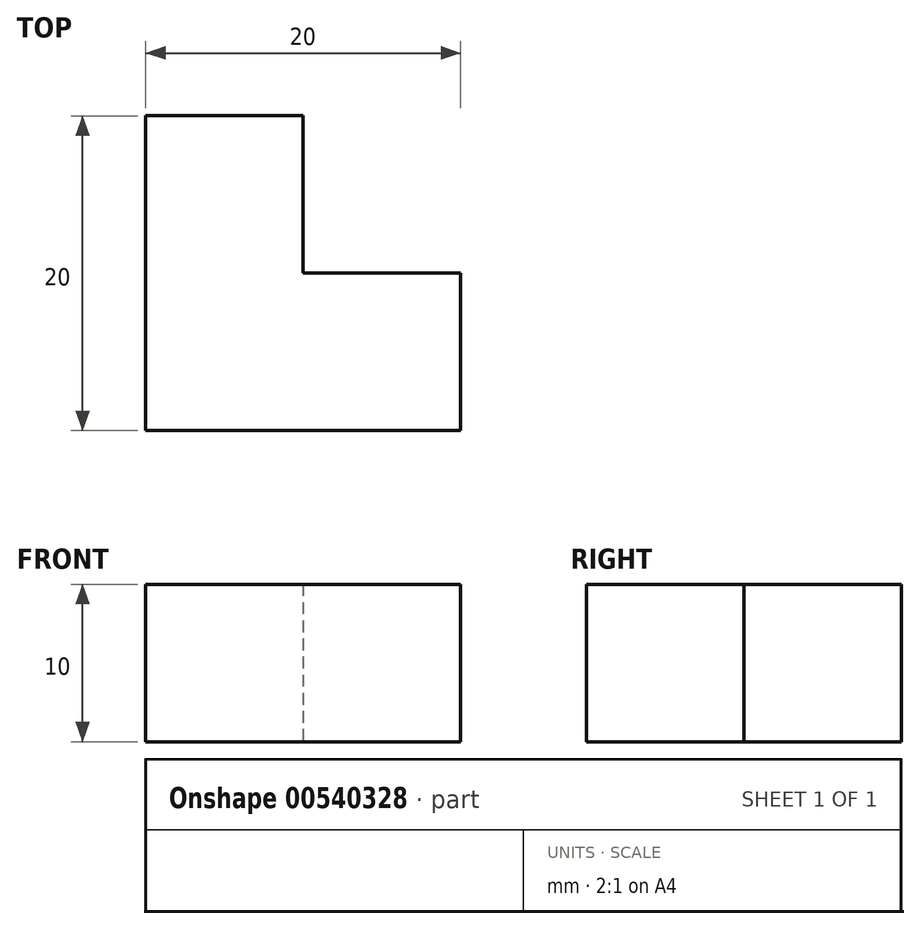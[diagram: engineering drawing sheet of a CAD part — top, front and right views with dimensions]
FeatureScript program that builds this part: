
annotation { "Feature Type Name" : "Feature", "Feature Type Description" : "" }
export const myFeature = defineFeature(function(context is Context, id is Id, definition is map)
    precondition{}
    {
        {
            var Q0;
            Q0=qCreatedBy(makeId("Top.planeOp"),FACE);
            var sketch = newSketch(context, id + "F0", { "sketchPlane" : qUnion([Q0])});
            skLineSegment(sketch, "E0", {"start": v(-20, 12.26) * mm, "end": v(-10, 12.26) * mm});
            skLineSegment(sketch, "E1", {"start": v(-10, 12.26) * mm, "end": v(-10, 2.26) * mm});
            skLineSegment(sketch, "E2", {"start": v(-10, 2.26) * mm, "end": v(0, 2.26) * mm});
            skLineSegment(sketch, "E3", {"start": v(0, 2.26) * mm, "end": v(0, -7.74) * mm});
            skLineSegment(sketch, "E4", {"start": v(0, -7.74) * mm, "end": v(-20, -7.74) * mm});
            skLineSegment(sketch, "E5", {"start": v(-20, -7.74) * mm, "end": v(-20, 12.26) * mm});
            skSolve(sketch);
        }
        {
            var Q0;
            Q0=makeQuery(id+"F0.imprint","IMPRINT",FACE,{"disambiguationData":[TD([[makeQuery(id+"F0.imprint","IMPRINT",EDGE,{"derivedFrom":sQuery(id+"F0.wireOp",EDGE,"E0")}),-1.0]])]});
            extrude(context, id + "F1", {"entities" : qUnion([Q0]), "depth" : 10 * mm, "offsetDistance" : 25 * mm});
        }
    });
